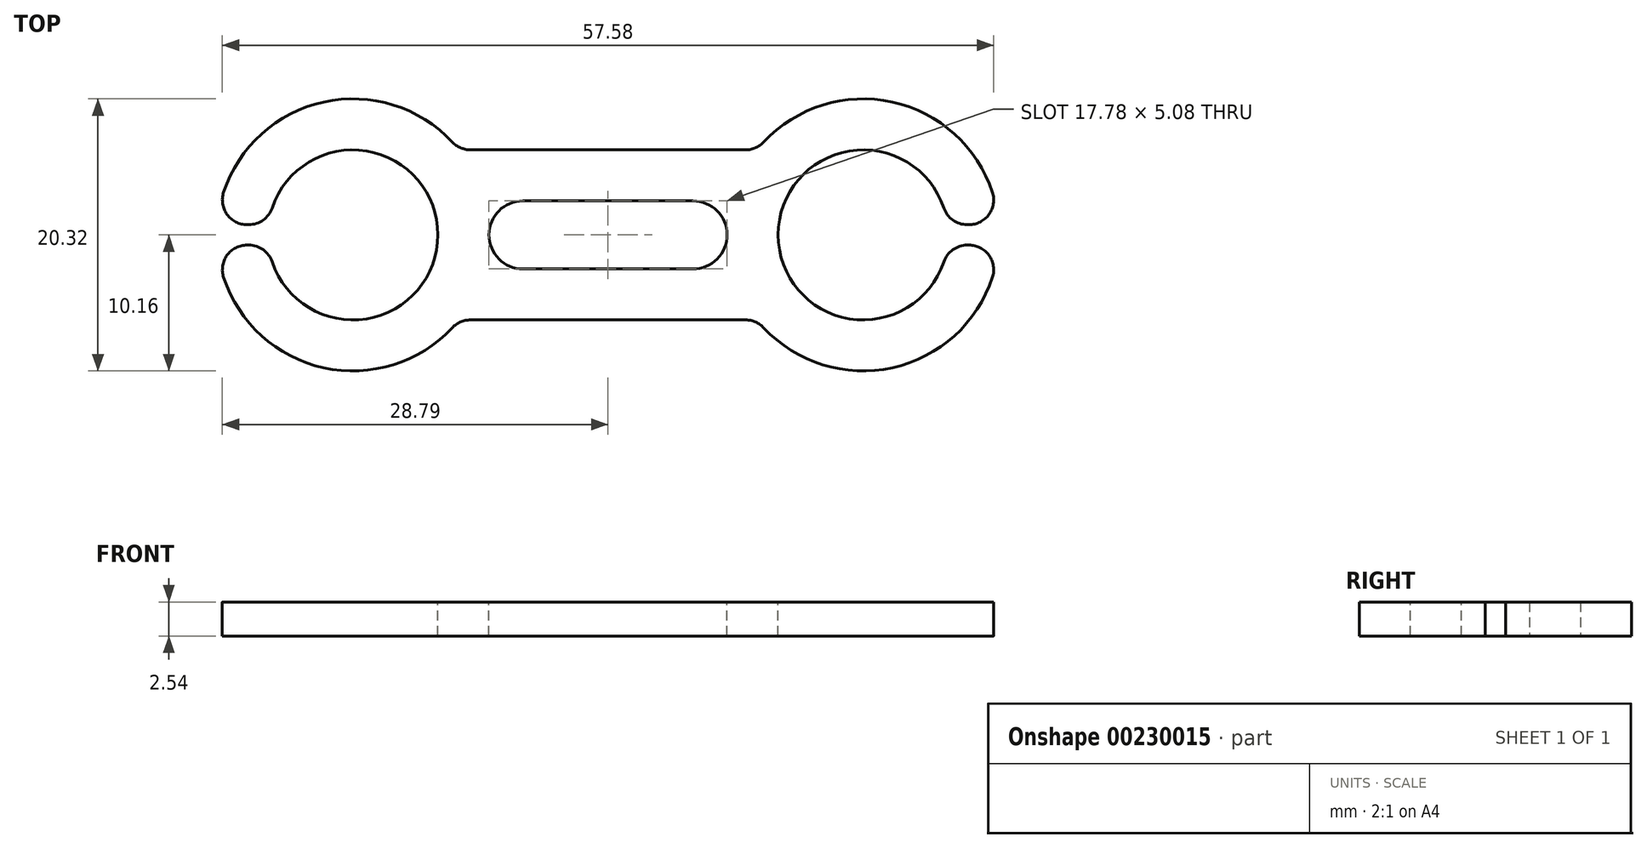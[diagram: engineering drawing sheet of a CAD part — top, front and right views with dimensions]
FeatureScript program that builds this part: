
annotation { "Feature Type Name" : "Feature", "Feature Type Description" : "" }
export const myFeature = defineFeature(function(context is Context, id is Id, definition is map)
    precondition{}
    {
        {
            var Q0;
            Q0=qCreatedBy(makeId("Top.planeOp"),FACE);
            var sketch = newSketch(context, id + "F0", { "sketchPlane" : qUnion([Q0])});
            skCircle(sketch, "E0", {"center": v(-19.05, 0) * mm, "radius": 10.16 * mm});
            skCircle(sketch, "E1", {"center": v(19.05, 0) * mm, "radius": 10.16 * mm});
            skLineSegment(sketch, "E2", {"start": v(-19.05, 0) * mm, "end": v(19.05, 0) * mm, "construction": true});
            skLineSegment(sketch, "E3", {"start": v(-19.05, 10.16) * mm, "end": v(19.05, 10.16) * mm, "construction": true});
            skLineSegment(sketch, "E4", {"start": v(19.05, -10.16) * mm, "end": v(-19.05, -10.16) * mm, "construction": true});
            skPoint(sketch, "E5", {"position": v(-13.97, 0) * mm});
            skPoint(sketch, "E6", {"position": v(-8.89, 0) * mm});
            skLineSegment(sketch, "E7.bottom", {"start": v(-11.12, 6.35) * mm, "end": v(11.12, 6.35) * mm});
            skLineSegment(sketch, "E7.top", {"start": v(-11.12, -6.35) * mm, "end": v(11.12, -6.35) * mm});
            skPoint(sketch, "E8", {"position": v(8.64, 0) * mm});
            skSolve(sketch);
        }
        {
            var Q0;
            Q0=qSketchRegion(id+"F0",true);
            extrude(context, id + "F1", {"entities" : qUnion([Q0]), "endBound" : BoundingType.SYMMETRIC, "depth" : 2.54 * mm});
        }
        {
            var Q0;
            Q0=makeQuery(id+"F1.opExtrude","CAP_FACE",FACE,{"disambiguationData":[OSD([sQuery(id+"F0.wireOp",EDGE,"E0"),sQuery(id+"F0.wireOp",EDGE,"E1"),sQuery(id+"F0.wireOp",EDGE,"JpsA0XJw-Zl1X-IY6a-TfOs-NOqodAkWJSI1")])],"isStart":false});
            var sketch = newSketch(context, id + "F2", { "sketchPlane" : qUnion([Q0])});
            skCircle(sketch, "E9", {"center": v(-19.05, 0) * mm, "radius": 6.35 * mm});
            skCircle(sketch, "E10", {"center": v(19.05, 0) * mm, "radius": 6.35 * mm});
            skSolve(sketch);
        }
        {
            var Q0;
            Q0=qSketchRegion(id+"F2",true);
            extrude(context, id + "F3", {"entities" : qUnion([Q0]), "operationType" : NewBodyOperationType.REMOVE, "oppositeDirection" : true, "depth" : 25.4 * mm});
        }
        {
            var Q0;
            Q0=makeQuery(id+"F1.opExtrude","CAP_FACE",FACE,{"disambiguationData":[OSD([sQuery(id+"F0.wireOp",EDGE,"E0"),sQuery(id+"F0.wireOp",EDGE,"E1"),sQuery(id+"F0.wireOp",EDGE,"JpsA0XJw-Zl1X-IY6a-TfOs-NOqodAkWJSI1")])],"isStart":false});
            var sketch = newSketch(context, id + "F4", { "sketchPlane" : qUnion([Q0])});
            skLineSegment(sketch, "E11", {"start": v(-19.05, 0) * mm, "end": v(-29.21, 0) * mm, "construction": true});
            skLineSegment(sketch, "E12.bottom", {"start": v(-29.21, 0.76) * mm, "end": v(-16.58, 0.76) * mm});
            skLineSegment(sketch, "E12.top", {"start": v(-29.21, -0.76) * mm, "end": v(-16.58, -0.76) * mm});
            skLineSegment(sketch, "E12.left", {"start": v(-29.21, 0.76) * mm, "end": v(-29.21, -0.76) * mm});
            skLineSegment(sketch, "E12.right", {"start": v(-16.58, 0.76) * mm, "end": v(-16.58, -0.76) * mm});
            skLineSegment(sketch, "E13", {"start": v(0, -0.63) * mm, "end": v(0, 19.69) * mm, "construction": true});
            skLineSegment(sketch, "E14.MirrorCS", {"start": v(16.58, 0.76) * mm, "end": v(16.58, -0.76) * mm});
            skLineSegment(sketch, "E15.MirrorCS", {"start": v(29.21, 0.76) * mm, "end": v(29.21, -0.76) * mm});
            skLineSegment(sketch, "E16.MirrorCS", {"start": v(19.05, 0) * mm, "end": v(29.21, 0) * mm, "construction": true});
            skLineSegment(sketch, "E17.MirrorCS", {"start": v(29.21, 0.76) * mm, "end": v(16.58, 0.76) * mm});
            skLineSegment(sketch, "E18.MirrorCS", {"start": v(29.21, -0.76) * mm, "end": v(16.58, -0.76) * mm});
            skSolve(sketch);
        }
        {
            var Q0;
            Q0=qSketchRegion(id+"F4",true);
            extrude(context, id + "F5", {"entities" : qUnion([Q0]), "operationType" : NewBodyOperationType.REMOVE, "oppositeDirection" : true, "depth" : 25.4 * mm});
        }
        {
            var Q0;
            Q0=makeQuery(id+"F5.boolean.opBoolean","INTERSECT",EDGE,{"derivedFrom":[makeQuery(id+"F1.opExtrude","SWEPT_FACE",FACE,{"disambiguationData":[OSD([sQuery(id+"F0.wireOp",EDGE,"E0")])]}),makeQuery(id+"F5.opExtrude","SWEPT_FACE",FACE,{"disambiguationData":[OSD([sQuery(id+"F4.wireOp",EDGE,"E12.bottom")])]})]});
            var Q1;
            Q1=makeQuery(id+"F5.boolean.opBoolean","INTERSECT",EDGE,{"derivedFrom":[makeQuery(id+"F3.boolean.opBoolean","COPY",FACE,{"derivedFrom":makeQuery(id+"F3.opExtrude","SWEPT_FACE",FACE,{"disambiguationData":[OSD([sQuery(id+"F2.wireOp",EDGE,"E9")])]})}),makeQuery(id+"F5.opExtrude","SWEPT_FACE",FACE,{"disambiguationData":[OSD([sQuery(id+"F4.wireOp",EDGE,"E12.bottom")])]})]});
            var Q2;
            Q2=makeQuery(id+"F5.boolean.opBoolean","INTERSECT",EDGE,{"derivedFrom":[makeQuery(id+"F3.boolean.opBoolean","COPY",FACE,{"derivedFrom":makeQuery(id+"F3.opExtrude","SWEPT_FACE",FACE,{"disambiguationData":[OSD([sQuery(id+"F2.wireOp",EDGE,"E9")])]})}),makeQuery(id+"F5.opExtrude","SWEPT_FACE",FACE,{"disambiguationData":[OSD([sQuery(id+"F4.wireOp",EDGE,"E12.top")])]})]});
            var Q3;
            Q3=makeQuery(id+"F5.boolean.opBoolean","INTERSECT",EDGE,{"derivedFrom":[makeQuery(id+"F1.opExtrude","SWEPT_FACE",FACE,{"disambiguationData":[OSD([sQuery(id+"F0.wireOp",EDGE,"E0")])]}),makeQuery(id+"F5.opExtrude","SWEPT_FACE",FACE,{"disambiguationData":[OSD([sQuery(id+"F4.wireOp",EDGE,"E12.top")])]})]});
            var Q4;
            Q4=makeQuery(id+"F5.boolean.opBoolean","INTERSECT",EDGE,{"derivedFrom":[makeQuery(id+"F3.boolean.opBoolean","COPY",FACE,{"derivedFrom":makeQuery(id+"F3.opExtrude","SWEPT_FACE",FACE,{"disambiguationData":[OSD([sQuery(id+"F2.wireOp",EDGE,"E10")])]})}),makeQuery(id+"F5.opExtrude","SWEPT_FACE",FACE,{"disambiguationData":[OSD([sQuery(id+"F4.wireOp",EDGE,"E18.MirrorCS")])]})]});
            var Q5;
            Q5=makeQuery(id+"F5.boolean.opBoolean","INTERSECT",EDGE,{"derivedFrom":[makeQuery(id+"F3.boolean.opBoolean","COPY",FACE,{"derivedFrom":makeQuery(id+"F3.opExtrude","SWEPT_FACE",FACE,{"disambiguationData":[OSD([sQuery(id+"F2.wireOp",EDGE,"E10")])]})}),makeQuery(id+"F5.opExtrude","SWEPT_FACE",FACE,{"disambiguationData":[OSD([sQuery(id+"F4.wireOp",EDGE,"E17.MirrorCS")])]})]});
            var Q6;
            Q6=makeQuery(id+"F5.boolean.opBoolean","INTERSECT",EDGE,{"derivedFrom":[makeQuery(id+"F1.opExtrude","SWEPT_FACE",FACE,{"disambiguationData":[OSD([sQuery(id+"F0.wireOp",EDGE,"E1")])]}),makeQuery(id+"F5.opExtrude","SWEPT_FACE",FACE,{"disambiguationData":[OSD([sQuery(id+"F4.wireOp",EDGE,"E17.MirrorCS")])]})]});
            var Q7;
            Q7=makeQuery(id+"F5.boolean.opBoolean","INTERSECT",EDGE,{"derivedFrom":[makeQuery(id+"F1.opExtrude","SWEPT_FACE",FACE,{"disambiguationData":[OSD([sQuery(id+"F0.wireOp",EDGE,"E1")])]}),makeQuery(id+"F5.opExtrude","SWEPT_FACE",FACE,{"disambiguationData":[OSD([sQuery(id+"F4.wireOp",EDGE,"E18.MirrorCS")])]})]});
            var Q8;
            Q8=makeQuery(id+"F1.opExtrude","SWEPT_EDGE",EDGE,{"disambiguationData":[OSD([sQuery(id+"F0.wireOp",EDGE,"E0"),sQuery(id+"F0.wireOp",EDGE,"E7.top")])]});
            var Q9;
            Q9=makeQuery(id+"F1.opExtrude","SWEPT_EDGE",EDGE,{"disambiguationData":[OSD([sQuery(id+"F0.wireOp",EDGE,"E1"),sQuery(id+"F0.wireOp",EDGE,"E7.top")])]});
            var Q10;
            Q10=makeQuery(id+"F1.opExtrude","SWEPT_EDGE",EDGE,{"disambiguationData":[OSD([sQuery(id+"F0.wireOp",EDGE,"E1"),sQuery(id+"F0.wireOp",EDGE,"E7.bottom")])]});
            var Q11;
            Q11=makeQuery(id+"F1.opExtrude","SWEPT_EDGE",EDGE,{"disambiguationData":[OSD([sQuery(id+"F0.wireOp",EDGE,"E0"),sQuery(id+"F0.wireOp",EDGE,"E7.bottom")])]});
            fillet(context, id + "F6", {"entities" : qUnion([Q0, Q1, Q2, Q3, Q4, Q5, Q6, Q7, Q8, Q9, Q10, Q11]), "radius" : 1.84 * mm, "tangentPropagation" : true, "allowEdgeOverflow" : false});
        }
        {
            var Q0;
            Q0=makeQuery(id+"F1.opExtrude","CAP_FACE",FACE,{"disambiguationData":[OSD([sQuery(id+"F0.wireOp",EDGE,"E0"),sQuery(id+"F0.wireOp",EDGE,"E1"),sQuery(id+"F0.wireOp",EDGE,"E7.bottom"),sQuery(id+"F0.wireOp",EDGE,"E7.top")])],"isStart":false});
            var sketch = newSketch(context, id + "F7", { "sketchPlane" : qUnion([Q0])});
            skArc(sketch, "E19", {"start": v(-9.21, -2.54) * mm, "mid": v(-8.89, 0) * mm, "end": v(-9.21, 2.54) * mm});
            skArc(sketch, "E20", {"start": v(9.21, 2.54) * mm, "mid": v(8.89, 0) * mm, "end": v(9.21, -2.54) * mm});
            skLineSegment(sketch, "E21", {"start": v(-9.21, 2.54) * mm, "end": v(9.21, 2.54) * mm});
            skLineSegment(sketch, "E22", {"start": v(-9.21, -2.54) * mm, "end": v(9.21, -2.54) * mm});
            skSolve(sketch);
        }
        {
            var Q0;
            Q0 = qSketchRegion(id + "F7", true);
            extrude(context, id + "F8", {"entities" : qUnion([Q0]), "operationType" : NewBodyOperationType.REMOVE, "oppositeDirection" : true, "depth" : 25.4 * mm});
        }
        {
            var Q0;
            Q0=makeQuery(id+"F8.boolean.opBoolean","COPY",EDGE,{"derivedFrom":makeQuery(id+"F8.opExtrude","SWEPT_EDGE",EDGE,{"disambiguationData":[OSD([sQuery(id+"F7.wireOp",EDGE,"E19"),sQuery(id+"F7.wireOp",EDGE,"E22")])]})});
            var Q1;
            Q1=makeQuery(id+"F8.boolean.opBoolean","COPY",EDGE,{"derivedFrom":makeQuery(id+"F8.opExtrude","SWEPT_EDGE",EDGE,{"disambiguationData":[OSD([sQuery(id+"F7.wireOp",EDGE,"E19"),sQuery(id+"F7.wireOp",EDGE,"E21")])]})});
            var Q2;
            Q2=makeQuery(id+"F8.boolean.opBoolean","COPY",EDGE,{"derivedFrom":makeQuery(id+"F8.opExtrude","SWEPT_EDGE",EDGE,{"disambiguationData":[OSD([sQuery(id+"F7.wireOp",EDGE,"E20"),sQuery(id+"F7.wireOp",EDGE,"E21")])]})});
            var Q3;
            Q3=makeQuery(id+"F8.boolean.opBoolean","COPY",EDGE,{"derivedFrom":makeQuery(id+"F8.opExtrude","SWEPT_EDGE",EDGE,{"disambiguationData":[OSD([sQuery(id+"F7.wireOp",EDGE,"E20"),sQuery(id+"F7.wireOp",EDGE,"E22")])]})});
            fillet(context, id + "F9", {"entities" : qUnion([Q0, Q1, Q2, Q3]), "radius" : 2.54 * mm, "tangentPropagation" : true, "allowEdgeOverflow" : false});
        }
    });
